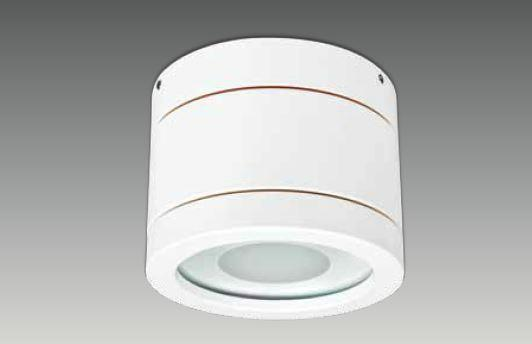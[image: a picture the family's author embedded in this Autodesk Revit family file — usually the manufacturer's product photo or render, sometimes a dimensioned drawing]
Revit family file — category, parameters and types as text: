
# Revit family: DS 1015 ROL
name_source: partatom
category: Lighting Fixtures
revit_build: Autodesk Revit 2017 (Build: 20160225_1515(x64)
units: mm (PartAtom-declared; Revit-internal decimal feet)

## family parameters
Cut with Voids When Loaded = No
Host = Face
Light Source = Yes
Part Type = Normal
Room Calculation Point = No
Round Connector Dimension = Use Diameter
Shared = No

## types (2) — shared parameters
Apparent Load = 10 VA
Color Filter = 16777215
Default Elevation = 1219 mm
Dimming Lamp Color Temperature Shift = <None>
Emit Shape Visible in Rendering = Yes
Emit from Circle Diameter = 115 mm  [stored 0.377297 ft]
Light Source Symbol Size = 610 mm
Manufacturer = ARLIGHT
Type Image = DS 1015 ROL.JPG
Wattage Comments = 10W

## type names (no varying parameters)
- DSROL.150.10.30
- DSROL.150.10.40

note: [stored X ft] marks values corroborated as IEEE doubles in the binary element streams (Revit-internal decimal feet)

## geometry (parser evidence)
native form markers: Sweep x2
no freeform markers — native parametric forms only
